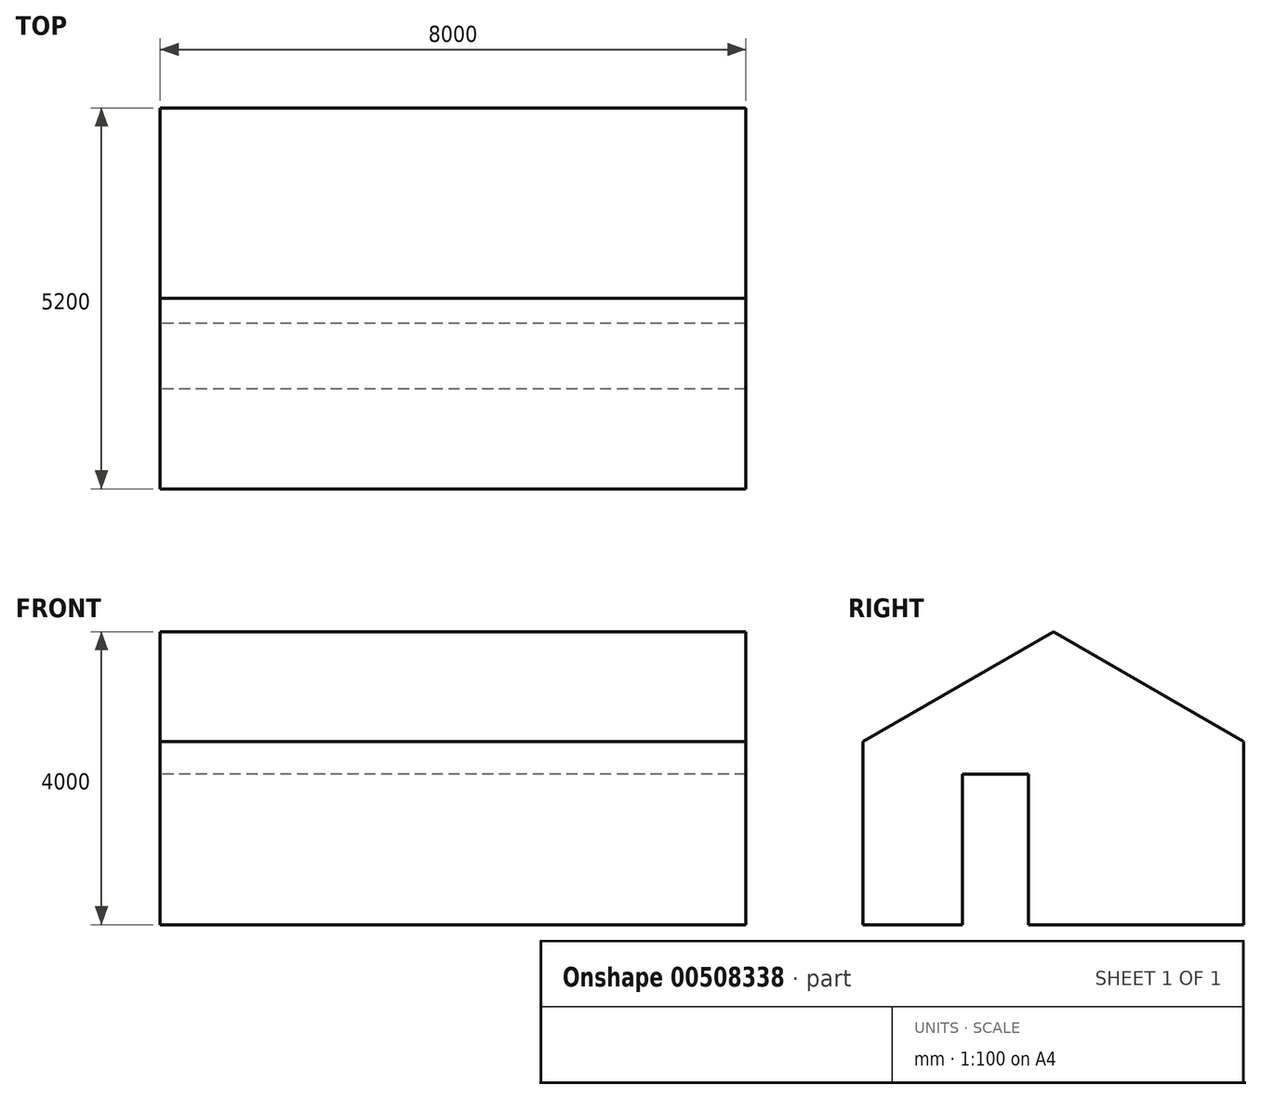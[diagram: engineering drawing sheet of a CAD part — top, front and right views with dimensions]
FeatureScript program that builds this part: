
annotation { "Feature Type Name" : "Feature", "Feature Type Description" : "" }
export const myFeature = defineFeature(function(context is Context, id is Id, definition is map)
    precondition{}
    {
        {
            var Q0;
            Q0=qCreatedBy(makeId("Right.planeOp"),FACE);
            var sketch = newSketch(context, id + "F0", { "sketchPlane" : qUnion([Q0])});
            skLineSegment(sketch, "E0.top", {"start": v(2600, -1250) * mm, "end": v(-2600, -1250) * mm});
            skLineSegment(sketch, "E0.left", {"start": v(2600, 1250) * mm, "end": v(2600, -1250) * mm});
            skLineSegment(sketch, "E0.right", {"start": v(-2600, 1250) * mm, "end": v(-2600, -1250) * mm});
            skPoint(sketch, "E0.middle", {"position": v(0, 0) * mm});
            skPoint(sketch, "E1.endSnap0", {"position": v(0, 1250) * mm});
            skLineSegment(sketch, "E2", {"start": v(2600, 1250) * mm, "end": v(0, 2750) * mm});
            skLineSegment(sketch, "E3", {"start": v(-2600, 1250) * mm, "end": v(0, 2750) * mm});
            skLineSegment(sketch, "E4.bottom", {"start": v(-1240, -1250) * mm, "end": v(-340, -1250) * mm});
            skLineSegment(sketch, "E4.top", {"start": v(-1240, 805) * mm, "end": v(-340, 805) * mm});
            skLineSegment(sketch, "E4.left", {"start": v(-1240, -1250) * mm, "end": v(-1240, 805) * mm});
            skLineSegment(sketch, "E4.right", {"start": v(-340, -1250) * mm, "end": v(-340, 805) * mm});
            skLineSegment(sketch, "E5.bottom", {"start": v(550, 805) * mm, "end": v(1800, 805) * mm});
            skLineSegment(sketch, "E5.top", {"start": v(550, -95) * mm, "end": v(1800, -95) * mm});
            skLineSegment(sketch, "E5.left", {"start": v(550, 805) * mm, "end": v(550, -95) * mm});
            skLineSegment(sketch, "E5.right", {"start": v(1800, 805) * mm, "end": v(1800, -95) * mm});
            skSolve(sketch);
        }
        {
            var Q0;
            {var subQ2=sQuery(id+"F0.wireOp",EDGE,"E0.left");Q0=makeQuery(id+"F0.imprint","IMPRINT",FACE,{"disambiguationData":[TD([[makeQuery(id+"F0.imprint","IMPRINT",EDGE,{"derivedFrom":subQ2}),-1.0]])]});}
            var Q1;
            Q1=makeQuery(id+"F0.imprint","IMPRINT",FACE,{"disambiguationData":[TD([[makeQuery(id+"F0.imprint","IMPRINT",EDGE,{"derivedFrom":sQuery(id+"F0.wireOp",EDGE,"E4.bottom")}),1.0]])]});
            var Q2;
            Q2=makeQuery(id+"F0.imprint","IMPRINT",FACE,{"disambiguationData":[TD([[makeQuery(id+"F0.imprint","IMPRINT",EDGE,{"derivedFrom":sQuery(id+"F0.wireOp",EDGE,"E5.bottom")}),-1.0]])]});
            extrude(context, id + "F1", {"entities" : qUnion([Q0, Q1, Q2]), "depth" : 8000 * mm});
        }
        {
            var Q0;
            Q0=makeQuery(id+"F1.opExtrude","SWEPT_FACE",FACE,{"disambiguationData":[OSD([sQuery(id+"F0.wireOp",EDGE,"E0.right")])]});
            var sketch = newSketch(context, id + "F2", { "sketchPlane" : qUnion([Q0])});
            skPoint(sketch, "E6.endSnap0", {"position": v(0, 0) * mm});
            skLineSegment(sketch, "E7", {"start": v(100, -1250) * mm, "end": v(100, 750) * mm});
            skLineSegment(sketch, "E8", {"start": v(100, 750) * mm, "end": v(4100, 750) * mm});
            skLineSegment(sketch, "E9", {"start": v(4100, 750) * mm, "end": v(4100, -1250) * mm});
            skLineSegment(sketch, "E10", {"start": v(4100, -1250) * mm, "end": v(100, -1250) * mm});
            skSolve(sketch);
        }
        {
            var Q0;
            Q0=sQuery(id+"F2.wireOp",EDGE,"E8");
            var Q1;
            Q1=sQuery(id+"F2.wireOp",EDGE,"E9");
            var Q2;
            Q2=sQuery(id+"F2.wireOp",EDGE,"E7");
            var Q3;
            Q3=sQuery(id+"F2.wireOp",EDGE,"E10");
            extrude(context, id + "F3", {"bodyType" : ToolBodyType.SURFACE, "surfaceEntities" : qUnion([Q0, Q1, Q2, Q3]), "oppositeDirection" : true, "depth" : 100 * mm});
        }
    });
